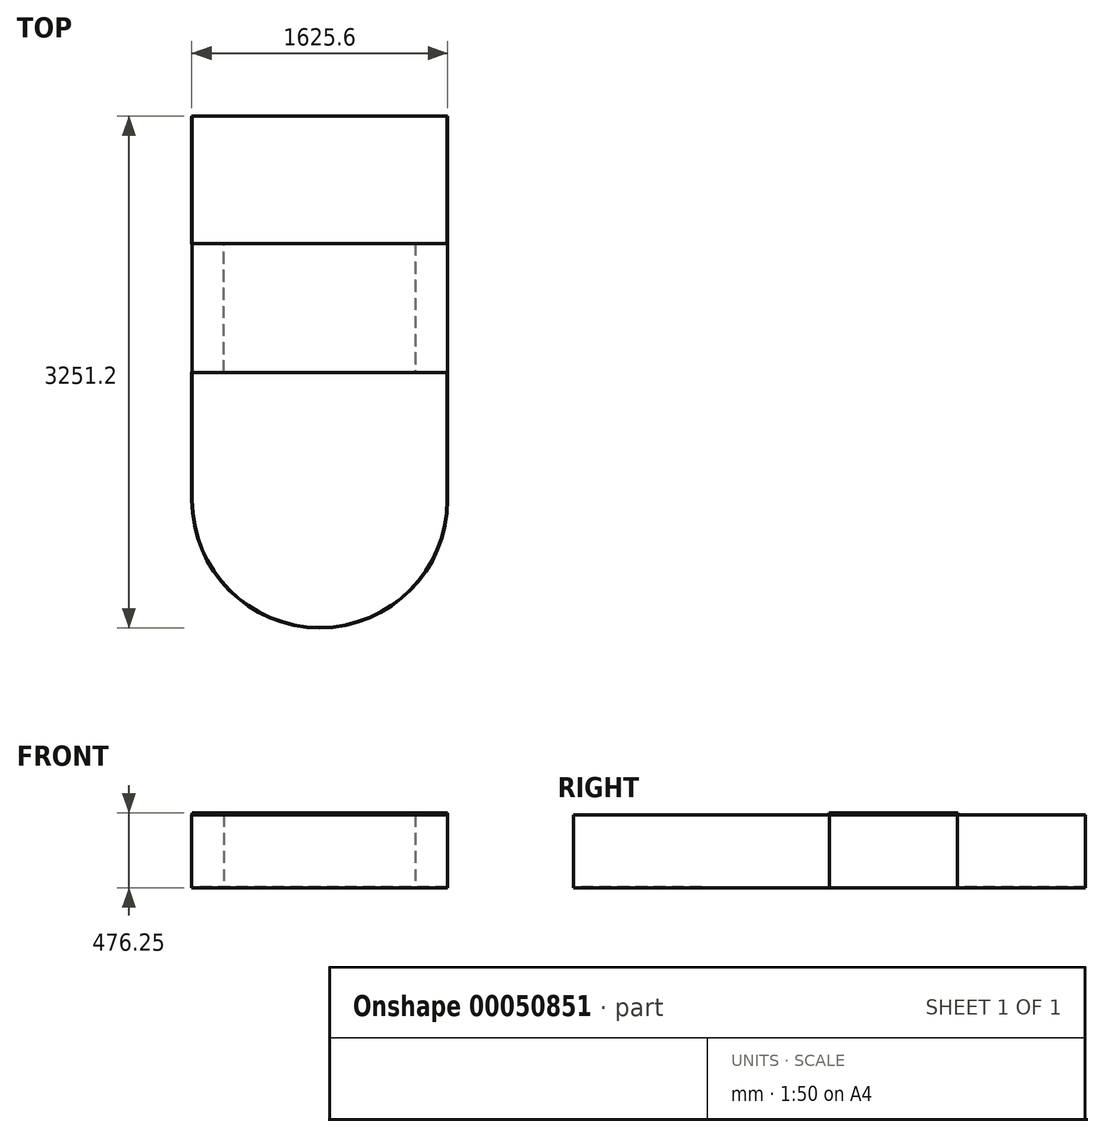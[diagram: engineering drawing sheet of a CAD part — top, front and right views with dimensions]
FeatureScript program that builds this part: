
annotation { "Feature Type Name" : "Feature", "Feature Type Description" : "" }
export const myFeature = defineFeature(function(context is Context, id is Id, definition is map)
    precondition{}
    {
        {
            var Q0;
            Q0=qCreatedBy(makeId("Top.planeOp"),FACE);
            var sketch = newSketch(context, id + "F0", { "sketchPlane" : qUnion([Q0])});
            skLineSegment(sketch, "E0.rect.bottom", {"start": v(812.8, 609.6) * mm, "end": v(-812.8, 609.6) * mm});
            skLineSegment(sketch, "E0.rect.left", {"start": v(812.8, 609.6) * mm, "end": v(812.8, -203.2) * mm});
            skLineSegment(sketch, "E0.rect.right", {"start": v(-812.8, 609.6) * mm, "end": v(-812.8, -203.2) * mm});
            skPoint(sketch, "E0.rect.middle", {"position": v(0, 0) * mm});
            skLineSegment(sketch, "E1.top", {"start": v(-812.8, -203.2) * mm, "end": v(-609.6, -203.2) * mm});
            skLineSegment(sketch, "E1.right", {"start": v(-609.6, -609.6) * mm, "end": v(-609.6, -203.2) * mm});
            skLineSegment(sketch, "E2.top", {"start": v(812.8, -203.2) * mm, "end": v(609.6, -203.2) * mm});
            skLineSegment(sketch, "E2.right", {"start": v(609.6, -609.6) * mm, "end": v(609.6, -203.2) * mm});
            skPoint(sketch, "E3.orphan", {"position": v(-812.8, -609.6) * mm});
            skPoint(sketch, "E4.orphan", {"position": v(812.8, -609.6) * mm});
            skLineSegment(sketch, "E5.MirrorCS", {"start": v(-609.6, -609.6) * mm, "end": v(-609.6, -1016) * mm});
            skLineSegment(sketch, "E6.MirrorCS", {"start": v(609.6, -609.6) * mm, "end": v(609.6, -1016) * mm});
            skLineSegment(sketch, "E7.MirrorCS", {"start": v(812.8, -1016) * mm, "end": v(609.6, -1016) * mm});
            skLineSegment(sketch, "E8.MirrorCS", {"start": v(-812.8, -1016) * mm, "end": v(-609.6, -1016) * mm});
            skLineSegment(sketch, "E9.MirrorCS", {"start": v(-812.8, -1828.8) * mm, "end": v(-812.8, -1016) * mm});
            skLineSegment(sketch, "E10.MirrorCS", {"start": v(812.8, -1828.8) * mm, "end": v(812.8, -1016) * mm});
            skArc(sketch, "E11", {"start": v(-812.8, -1828.8) * mm, "mid": v(0, -2641.6) * mm, "end": v(812.8, -1828.8) * mm});
            skSolve(sketch);
        }
        {
            var Q0;
            Q0=makeQuery(id+"F0.imprint","IMPRINT",FACE,{"disambiguationData":[TD([[makeQuery(id+"F0.imprint","IMPRINT",EDGE,{"derivedFrom":sQuery(id+"F0.wireOp",EDGE,"E0.rect.bottom")}),1.0]])]});
            extrude(context, id + "F1", {"entities" : qUnion([Q0]), "depth" : 6.35 * mm});
        }
        {
            var Q0;
            Q0=makeQuery(id+"F1.opExtrude","CAP_FACE",FACE,{"disambiguationData":[OSD([sQuery(id+"F0.wireOp",EDGE,"E0.rect.bottom"),sQuery(id+"F0.wireOp",EDGE,"E0.rect.left"),sQuery(id+"F0.wireOp",EDGE,"E0.rect.right"),sQuery(id+"F0.wireOp",EDGE,"E1.top"),sQuery(id+"F0.wireOp",EDGE,"E1.right"),sQuery(id+"F0.wireOp",EDGE,"E2.top"),sQuery(id+"F0.wireOp",EDGE,"E2.right"),sQuery(id+"F0.wireOp",EDGE,"E5.MirrorCS"),sQuery(id+"F0.wireOp",EDGE,"E6.MirrorCS"),sQuery(id+"F0.wireOp",EDGE,"E7.MirrorCS"),sQuery(id+"F0.wireOp",EDGE,"E8.MirrorCS"),sQuery(id+"F0.wireOp",EDGE,"E9.MirrorCS"),sQuery(id+"F0.wireOp",EDGE,"E10.MirrorCS"),sQuery(id+"F0.wireOp",EDGE,"E11")])],"isStart":false});
            var sketch = newSketch(context, id + "F2", { "sketchPlane" : qUnion([Q0])});
            skLineSegment(sketch, "E12.0", {"start": v(809.63, 609.6) * mm, "end": v(809.63, -200.02) * mm});
            skLineSegment(sketch, "E12.1", {"start": v(-809.62, -1019.18) * mm, "end": v(-606.42, -1019.18) * mm});
            skLineSegment(sketch, "E12.2", {"start": v(-606.42, -1019.18) * mm, "end": v(-606.42, -200.03) * mm});
            skLineSegment(sketch, "E12.3", {"start": v(-809.62, -200.03) * mm, "end": v(-606.42, -200.03) * mm});
            skLineSegment(sketch, "E12.4", {"start": v(-809.63, 609.6) * mm, "end": v(-809.62, -200.03) * mm});
            skLineSegment(sketch, "E12.5", {"start": v(-809.63, -1828.8) * mm, "end": v(-809.62, -1019.18) * mm});
            skArc(sketch, "E12.6", {"start": v(-809.63, -1828.8) * mm, "mid": v(0, -2638.43) * mm, "end": v(809.62, -1828.8) * mm});
            skLineSegment(sketch, "E12.7", {"start": v(809.63, -1828.8) * mm, "end": v(809.63, -1019.18) * mm});
            skLineSegment(sketch, "E12.8", {"start": v(809.63, -1019.18) * mm, "end": v(606.43, -1019.18) * mm});
            skLineSegment(sketch, "E12.9", {"start": v(606.43, -200.03) * mm, "end": v(606.43, -1019.18) * mm});
            skLineSegment(sketch, "E12.10", {"start": v(809.63, -200.02) * mm, "end": v(606.43, -200.02) * mm});
            skLineSegment(sketch, "E13", {"start": v(-809.63, 609.6) * mm, "end": v(-812.8, 609.6) * mm});
            skLineSegment(sketch, "E14", {"start": v(809.63, 609.6) * mm, "end": v(812.8, 609.6) * mm});
            skSolve(sketch);
        }
        {
            var Q0;
            Q0=makeQuery(id+"F2.imprint","IMPRINT",FACE,{"disambiguationData":[TD([[makeQuery(id+"F2.imprint","IMPRINT",EDGE,{"derivedFrom":sQuery(id+"F2.wireOp",EDGE,"E12.0")}),1.0]])]});
            extrude(context, id + "F3", {"entities" : qUnion([Q0]), "operationType" : NewBodyOperationType.ADD, "depth" : 457.2 * mm});
        }
        {
            var Q0;
            Q0=qCreatedBy(makeId("Top.planeOp"),FACE);
            cPlane(context, id + "F4", {"entities" : qUnion([Q0]), "cplaneType" : CPlaneType.OFFSET, "offset" : 463.55 * mm, "width" : 152.4 * mm, "height" : 152.4 * mm});
        }
        {
            var Q0;
            Q0=qCreatedBy(id+"F4.planeOp",FACE);
            var sketch = newSketch(context, id + "F5", { "sketchPlane" : qUnion([Q0])});
            skLineSegment(sketch, "E15.bottom", {"start": v(-812.78, -1019.17) * mm, "end": v(812.8, -1019.17) * mm});
            skLineSegment(sketch, "E15.top", {"start": v(-812.78, -200.02) * mm, "end": v(812.8, -200.02) * mm});
            skLineSegment(sketch, "E15.left", {"start": v(-812.78, -1019.17) * mm, "end": v(-812.78, -200.02) * mm});
            skLineSegment(sketch, "E15.right", {"start": v(812.8, -1019.17) * mm, "end": v(812.8, -200.02) * mm});
            skSolve(sketch);
        }
        {
            var Q0;
            Q0 = qSketchRegion(id + "F5", true);
            extrude(context, id + "F6", {"entities" : qUnion([Q0]), "operationType" : NewBodyOperationType.ADD, "depth" : 12.7 * mm});
        }
    });
